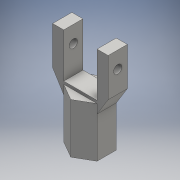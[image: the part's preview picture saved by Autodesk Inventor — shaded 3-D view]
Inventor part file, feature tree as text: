
AUTODESK INVENTOR PART (.ipt)
format: ipt  version: 2016 (Build 200138000, 138)  size: 146,944 bytes
history: native  units: mm
features: extrude x6, sketch x6
ambient origin geometry x8: Origin, YZ Plane, XZ Plane, XY Plane, X Axis, Y Axis, Z Axis, Center Point
bodies: Solid1 (feature_tree)
feature tree (12):
  extrude  "Extrusion1"  Depth=18.0mm TaperAngle=0.0deg
  extrude  "Extrusion2"  Depth=14.0mm TaperAngle=0.0deg
  extrude  "Extrusion3"  Depth=4.0mm
  extrude  "Extrusion4"  Depth=6.928203mm
  extrude  "Extrusion5"  Depth=6.928203mm TaperAngle=0.0deg
  extrude  "Extrusion6"  Depth=6.928203mm TaperAngle=0.0deg
  sketch  "Sketch1"  dims[d1=12.0mm d3=18.0mm d4=0.0mm]
  sketch  "Sketch2"  dims[d5=6.2mm d6=14.0mm d7=0.0mm]
  sketch  "Sketch3"  dims[d8=17.0mm d9=0.0mm d10=4.0mm]
  sketch  "Sketch4"  dims[d11=4.0mm d12=6.928203mm]
  sketch  "Sketch5"  dims[d13=6.928203mm d14=0.0mm d15=6.928203mm d16=0.0mm]
  sketch  "Sketch6"  dims[d18=3.0mm d19=6.928203mm d20=0.0mm]
